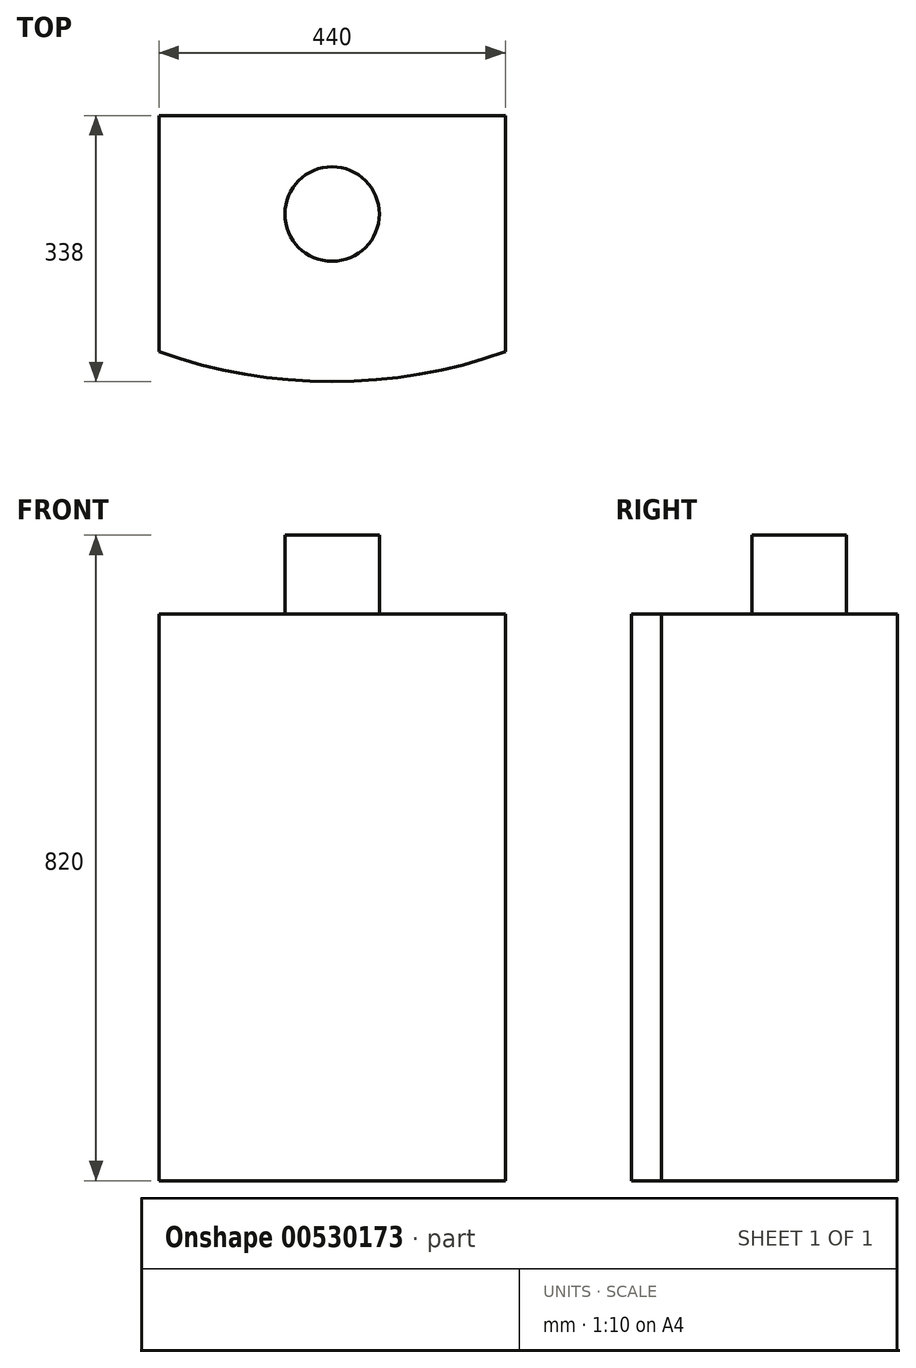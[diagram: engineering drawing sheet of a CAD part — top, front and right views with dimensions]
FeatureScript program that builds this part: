
annotation { "Feature Type Name" : "Feature", "Feature Type Description" : "" }
export const myFeature = defineFeature(function(context is Context, id is Id, definition is map)
    precondition{}
    {
        {
            var Q0;
            Q0=qCreatedBy(makeId("Top.planeOp"),FACE);
            var sketch = newSketch(context, id + "F0", { "sketchPlane" : qUnion([Q0])});
            skLineSegment(sketch, "E0", {"start": v(-220, -300) * mm, "end": v(-220, 0) * mm});
            skLineSegment(sketch, "E1", {"start": v(-220, 0) * mm, "end": v(220, 0) * mm});
            skLineSegment(sketch, "E2", {"start": v(220, 0) * mm, "end": v(220, -300) * mm});
            skArc(sketch, "E3", {"start": v(-220, -300) * mm, "mid": v(0, -338) * mm, "end": v(220, -300) * mm});
            skSolve(sketch);
        }
        {
            var Q0;
            Q0=makeQuery(id+"F0.imprint","IMPRINT",FACE,{"disambiguationData":[TD([[makeQuery(id+"F0.imprint","IMPRINT",EDGE,{"derivedFrom":sQuery(id+"F0.wireOp",EDGE,"E0")}),-1.0]])]});
            extrude(context, id + "F1", {"entities" : qUnion([Q0]), "depth" : 720 * mm, "offsetDistance" : 25 * mm});
        }
        {
            var Q0;
            Q0=makeQuery(id+"F1.opExtrude","CAP_FACE",FACE,{"disambiguationData":[OSD([sQuery(id+"F0.wireOp",EDGE,"E0"),sQuery(id+"F0.wireOp",EDGE,"E1"),sQuery(id+"F0.wireOp",EDGE,"E2"),sQuery(id+"F0.wireOp",EDGE,"E3")])],"isStart":false});
            var sketch = newSketch(context, id + "F2", { "sketchPlane" : qUnion([Q0])});
            skCircle(sketch, "E4", {"center": v(0, -125) * mm, "radius": 60 * mm});
            skSolve(sketch);
        }
        {
            var Q0;
            Q0=makeQuery(id+"F2.imprint","IMPRINT",FACE,{"disambiguationData":[TD([[makeQuery(id+"F2.imprint","IMPRINT",EDGE,{"derivedFrom":sQuery(id+"F2.wireOp",EDGE,"E4")}),1.0]])]});
            extrude(context, id + "F3", {"entities" : qUnion([Q0]), "operationType" : NewBodyOperationType.ADD, "depth" : 100 * mm, "offsetDistance" : 25 * mm});
        }
    });
